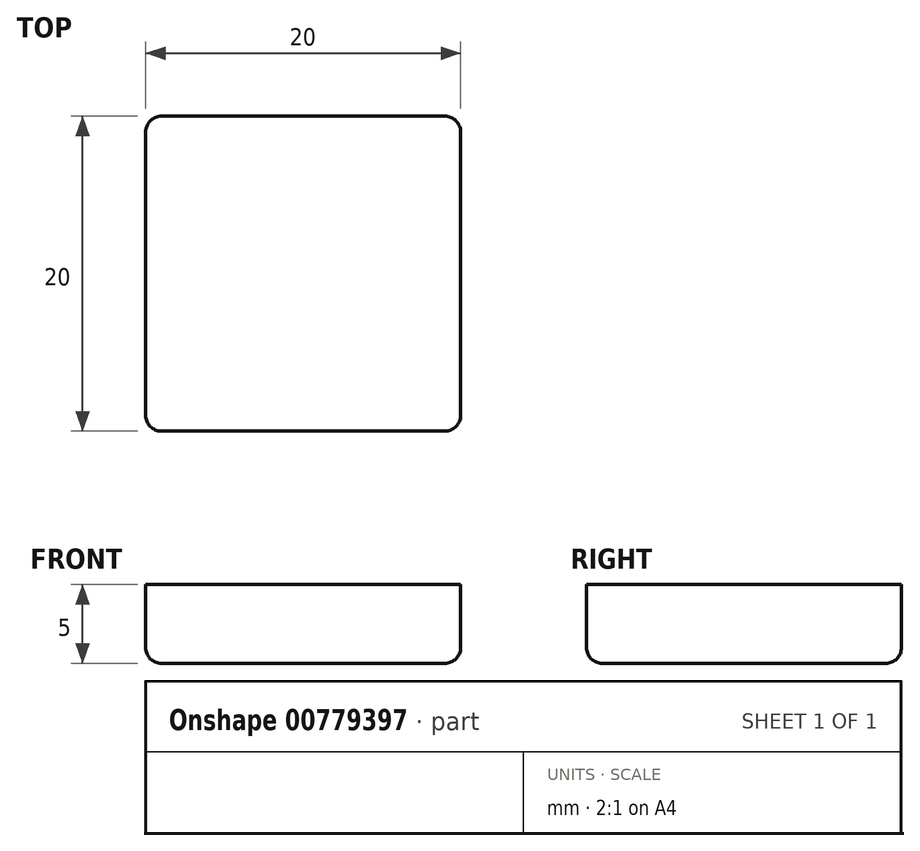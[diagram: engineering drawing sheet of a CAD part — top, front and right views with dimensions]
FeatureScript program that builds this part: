
annotation { "Feature Type Name" : "Feature", "Feature Type Description" : "" }
export const myFeature = defineFeature(function(context is Context, id is Id, definition is map)
    precondition{}
    {
        {
            var Q0;
            Q0=qCreatedBy(makeId("Top.planeOp"),FACE);
            var sketch = newSketch(context, id + "F0", { "sketchPlane" : qUnion([Q0])});
            skLineSegment(sketch, "E0.bottom", {"start": v(9, -10) * mm, "end": v(-9, -10) * mm});
            skLineSegment(sketch, "E0.top", {"start": v(9, 10) * mm, "end": v(-9, 10) * mm});
            skLineSegment(sketch, "E0.left", {"start": v(10, -9) * mm, "end": v(10, 9) * mm});
            skLineSegment(sketch, "E0.right", {"start": v(-10, -9) * mm, "end": v(-10, 9) * mm});
            skPoint(sketch, "E0.middle", {"position": v(0, 0) * mm});
            skPoint(sketch, "E1.visualSharp", {"position": v(-10, -10) * mm});
            skArc(sketch, "E1.filletArc", {"start": v(-10, -9) * mm, "mid": v(-9.7, -9.7) * mm, "end": v(-9, -10) * mm});
            skPoint(sketch, "E2.visualSharp", {"position": v(-10, 10) * mm});
            skArc(sketch, "E2.filletArc", {"start": v(-9, 10) * mm, "mid": v(-9.7, 9.7) * mm, "end": v(-10, 9) * mm});
            skPoint(sketch, "E3.visualSharp", {"position": v(10, 10) * mm});
            skArc(sketch, "E3.filletArc", {"start": v(10, 9) * mm, "mid": v(9.7, 9.7) * mm, "end": v(9, 10) * mm});
            skPoint(sketch, "E4.visualSharp", {"position": v(10, -10) * mm});
            skArc(sketch, "E4.filletArc", {"start": v(9, -10) * mm, "mid": v(9.7, -9.7) * mm, "end": v(10, -9) * mm});
            skSolve(sketch);
        }
        {
            var Q0;
            Q0=makeQuery(id+"F0.imprint","IMPRINT",FACE,{"disambiguationData":[TD([[makeQuery(id+"F0.imprint","IMPRINT",EDGE,{"derivedFrom":sQuery(id+"F0.wireOp",EDGE,"E0.bottom")}),-1.0]])]});
            extrude(context, id + "F1", {"entities" : qUnion([Q0]), "depth" : 5 * mm, "offsetDistance" : 25 * mm});
        }
        {
            var Q0;
            Q0=makeQuery(id+"F1.opExtrude","CAP_FACE",FACE,{"disambiguationData":[OSD([sQuery(id+"F0.wireOp",EDGE,"E0.bottom"),sQuery(id+"F0.wireOp",EDGE,"E0.top"),sQuery(id+"F0.wireOp",EDGE,"E0.left"),sQuery(id+"F0.wireOp",EDGE,"E0.right"),sQuery(id+"F0.wireOp",EDGE,"E1.filletArc"),sQuery(id+"F0.wireOp",EDGE,"E2.filletArc"),sQuery(id+"F0.wireOp",EDGE,"E3.filletArc"),sQuery(id+"F0.wireOp",EDGE,"E4.filletArc")])],"isStart":true});
            fillet(context, id + "F2", {"entities" : qUnion([Q0]), "radius" : 1 * mm, "tangentPropagation" : true, "allowEdgeOverflow" : false});
        }
    });
